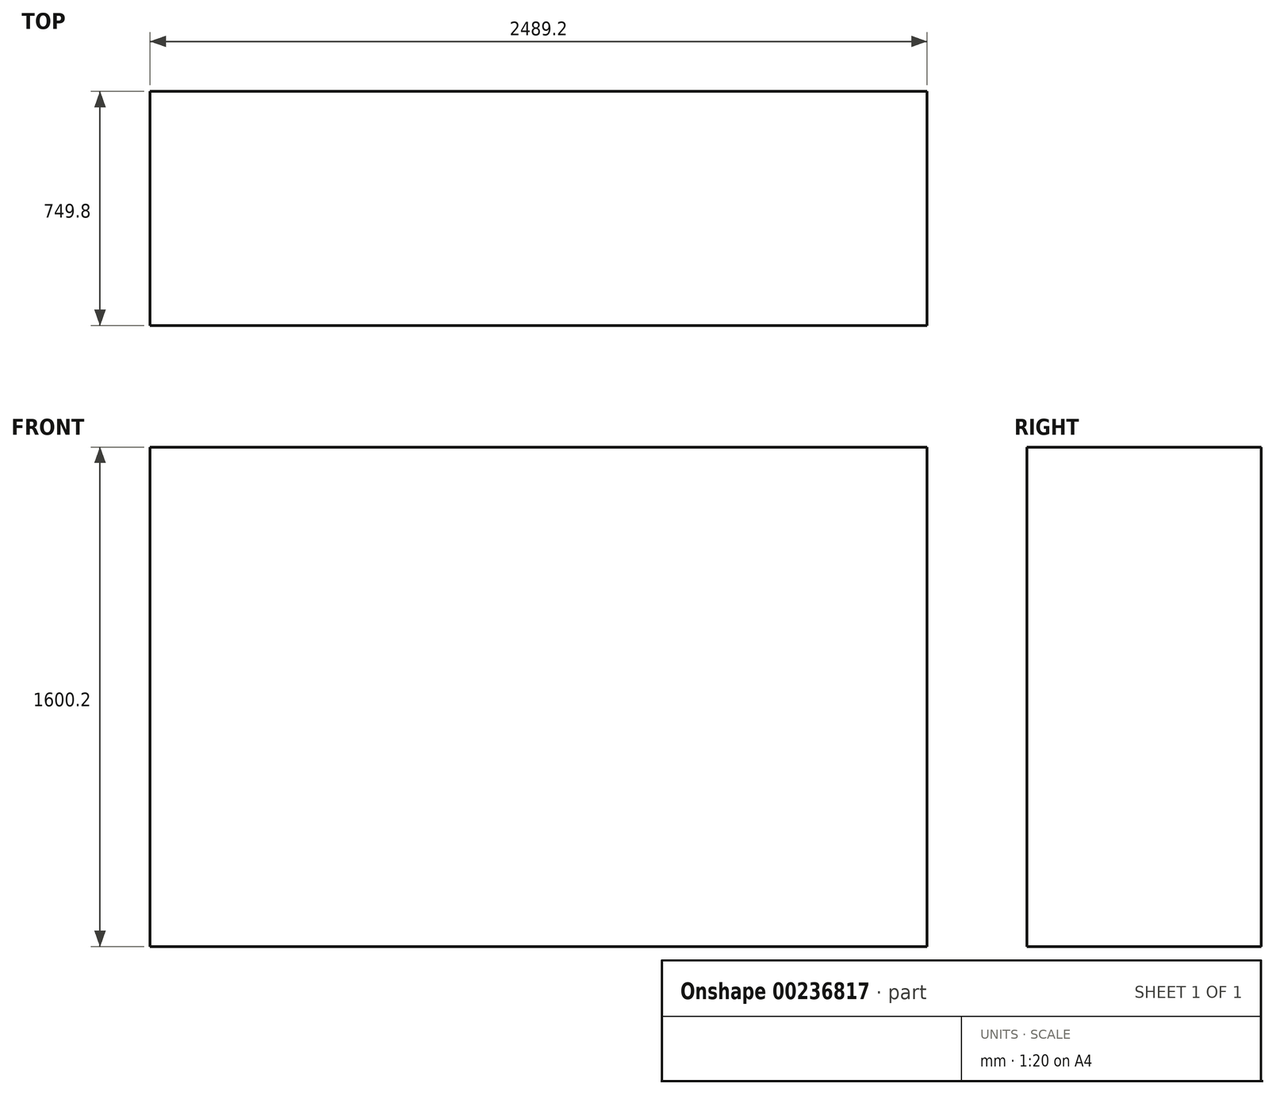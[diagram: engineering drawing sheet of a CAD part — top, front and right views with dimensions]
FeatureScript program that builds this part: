
annotation { "Feature Type Name" : "Feature", "Feature Type Description" : "" }
export const myFeature = defineFeature(function(context is Context, id is Id, definition is map)
    precondition{}
    {
        {
            var Q0;
            Q0=qCreatedBy(makeId("Top.planeOp"),FACE);
            var sketch = newSketch(context, id + "F0", { "sketchPlane" : qUnion([Q0])});
            skLineSegment(sketch, "E0.bottom", {"start": v(-1244.6, 374.9) * mm, "end": v(1244.6, 374.9) * mm});
            skLineSegment(sketch, "E0.top", {"start": v(-1244.6, -374.9) * mm, "end": v(1244.6, -374.9) * mm});
            skLineSegment(sketch, "E0.left", {"start": v(-1244.6, 374.9) * mm, "end": v(-1244.6, -374.9) * mm});
            skLineSegment(sketch, "E0.right", {"start": v(1244.6, 374.9) * mm, "end": v(1244.6, -374.9) * mm});
            skPoint(sketch, "E0.middle", {"position": v(0, 0) * mm});
            skSolve(sketch);
        }
        {
            var Q0;
            Q0=makeQuery(id+"F0.imprint","IMPRINT",FACE,{"disambiguationData":[TD([[makeQuery(id+"F0.imprint","IMPRINT",EDGE,{"derivedFrom":sQuery(id+"F0.wireOp",EDGE,"E0.bottom")}),-1.0]])]});
            extrude(context, id + "F1", {"entities" : qUnion([Q0]), "depth" : 1600.2 * mm});
        }
    });
